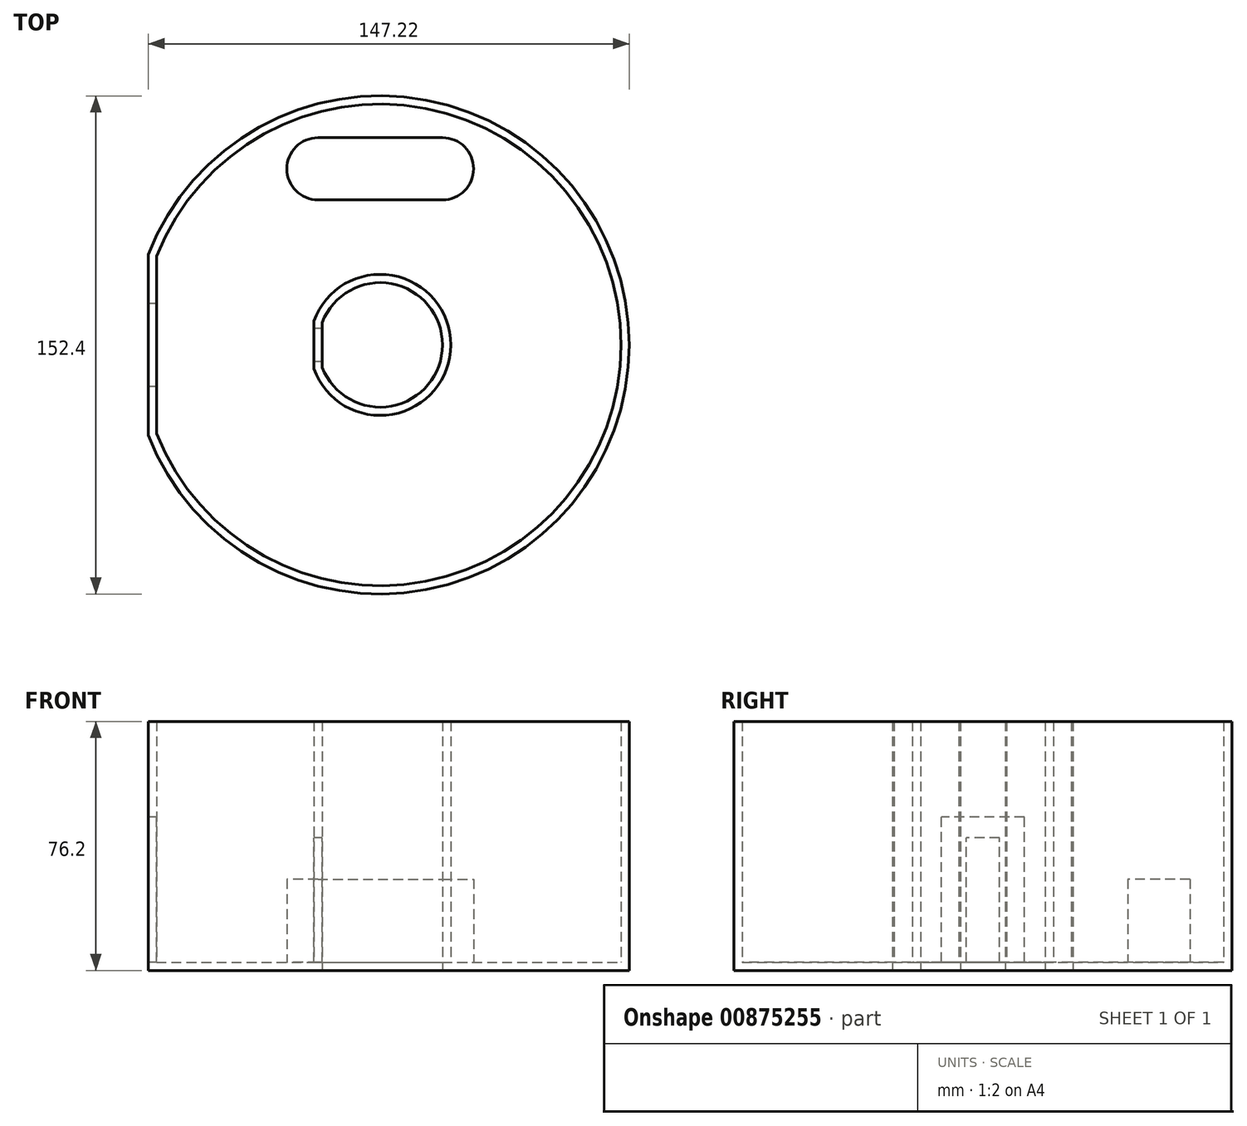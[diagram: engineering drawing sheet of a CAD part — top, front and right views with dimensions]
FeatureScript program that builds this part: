
annotation { "Feature Type Name" : "Feature", "Feature Type Description" : "" }
export const myFeature = defineFeature(function(context is Context, id is Id, definition is map)
    precondition{}
    {
        {
            var Q0;
            Q0=qCreatedBy(makeId("Top.planeOp"),FACE);
            var sketch = newSketch(context, id + "F0", { "sketchPlane" : qUnion([Q0])});
            skCircle(sketch, "E0", {"center": v(0, 0) * mm, "radius": 76.2 * mm});
            skCircle(sketch, "E1", {"center": v(0, 0) * mm, "radius": 19.05 * mm});
            skLineSegment(sketch, "E2", {"start": v(-71.02, 27.6) * mm, "end": v(-71.02, -27.6) * mm});
            skLineSegment(sketch, "E3", {"start": v(-17.77, 6.86) * mm, "end": v(-17.77, -6.86) * mm});
            skPoint(sketch, "E4.endSnap0", {"position": v(-17.77, 0) * mm});
            skSolve(sketch);
        }
        {
            var Q0;
            Q0=makeQuery(id+"F0.imprint","IMPRINT",FACE,{"disambiguationData":[TD([[makeQuery(id+"F0.imprint","IMPRINT",EDGE,{"derivedFrom":sQuery(id+"F0.wireOp",EDGE,"E1")}),-1.0]])]});
            var Q1;
            {var subQ0=sQuery(id+"F0.wireOp",EDGE,"E3");Q1=makeQuery(id+"F0.imprint","IMPRINT",FACE,{"disambiguationData":[TD([[makeQuery(id+"F0.imprint","IMPRINT",EDGE,{"derivedFrom":subQ0}),-1.0]])]});}
            extrude(context, id + "F1", {"entities" : qUnion([Q0, Q1]), "depth" : 76.2 * mm, "offsetDistance" : 25.4 * mm});
        }
        {
            var Q0;
            Q0=makeQuery(id+"F1.opExtrude","CAP_FACE",FACE,{"disambiguationData":[OSD([sQuery(id+"F0.wireOp",EDGE,"E0"),sQuery(id+"F0.wireOp",EDGE,"E1")])],"isStart":false});
            shell(context, id + "F2", {"entities" : qUnion([Q0]), "thickness" : 2.54 * mm});
        }
        {
            var Q0;
            {var subQ0=sQuery(id+"F0.wireOp",EDGE,"E1");var subQ1=sQuery(id+"F0.wireOp",EDGE,"E0");Q0=makeQuery(id+"F2.opShell","OFFSET_FACE",FACE,{"disambiguationData":[OSD([subQ1,subQ0]),TDD([makeQuery(id+"F1.opExtrude","CAP_FACE",FACE,{"disambiguationData":[OSD([subQ1,subQ0])],"isStart":true})])]});}
            var sketch = newSketch(context, id + "F3", { "sketchPlane" : qUnion([Q0])});
            skLineSegment(sketch, "E5.bottom", {"start": v(-19.05, 63.4) * mm, "end": v(19.05, 63.4) * mm});
            skLineSegment(sketch, "E5.top", {"start": v(-19.05, 44.35) * mm, "end": v(19.05, 44.35) * mm});
            skLineSegment(sketch, "E5.left", {"start": v(-19.05, 63.4) * mm, "end": v(-19.05, 44.35) * mm});
            skLineSegment(sketch, "E5.right", {"start": v(19.05, 63.4) * mm, "end": v(19.05, 44.35) * mm});
            skCircle(sketch, "E6", {"center": v(-19.05, 53.88) * mm, "radius": 9.53 * mm});
            skCircle(sketch, "E7", {"center": v(19.05, 53.88) * mm, "radius": 9.53 * mm});
            skLineSegment(sketch, "E8", {"start": v(0, 0) * mm, "end": v(0, 44.35) * mm});
            skLineSegment(sketch, "E9", {"start": v(0, 0) * mm, "end": v(0, -30.53) * mm});
            skSolve(sketch);
        }
        {
            var Q0;
            Q0 = qSketchRegion(id + "F3", true);
            extrude(context, id + "F4", {"entities" : qUnion([Q0]), "operationType" : NewBodyOperationType.ADD, "depth" : 25.4 * mm, "offsetDistance" : 25.4 * mm});
        }
        {
            var Q0;
            Q0=makeQuery(id+"F1.opExtrude","SWEPT_FACE",FACE,{"disambiguationData":[OSD([sQuery(id+"F0.wireOp",EDGE,"E2")])]});
            var sketch = newSketch(context, id + "F5", { "sketchPlane" : qUnion([Q0])});
            skLineSegment(sketch, "E10.bottom", {"start": v(-12.7, 0) * mm, "end": v(12.7, 0) * mm});
            skLineSegment(sketch, "E10.top", {"start": v(-12.7, 2.54) * mm, "end": v(12.7, 2.54) * mm});
            skLineSegment(sketch, "E10.left", {"start": v(-12.7, 0) * mm, "end": v(-12.7, 2.54) * mm});
            skLineSegment(sketch, "E10.right", {"start": v(12.7, 0) * mm, "end": v(12.7, 2.54) * mm});
            skLineSegment(sketch, "E11.top", {"start": v(-12.7, 47) * mm, "end": v(12.7, 47) * mm});
            skLineSegment(sketch, "E11.left", {"start": v(-12.7, 2.54) * mm, "end": v(-12.7, 47) * mm});
            skLineSegment(sketch, "E11.right", {"start": v(12.7, 2.54) * mm, "end": v(12.7, 47) * mm});
            skSolve(sketch);
        }
        {
            var Q0;
            Q0=makeQuery(id+"F5.imprint","IMPRINT",FACE,{"disambiguationData":[TD([[makeQuery(id+"F5.imprint","IMPRINT",EDGE,{"derivedFrom":sQuery(id+"F5.wireOp",EDGE,"E10.top")}),1.0]])]});
            extrude(context, id + "F6", {"entities" : qUnion([Q0]), "operationType" : NewBodyOperationType.REMOVE, "oppositeDirection" : true, "depth" : 2.54 * mm, "offsetDistance" : 25.4 * mm});
        }
        {
            var Q0;
            Q0=makeQuery(id+"F2.opShell","OFFSET_FACE",FACE,{"disambiguationData":[OSD([sQuery(id+"F0.wireOp",EDGE,"E3")])]});
            var sketch = newSketch(context, id + "F7", { "sketchPlane" : qUnion([Q0])});
            skLineSegment(sketch, "E12.bottom", {"start": v(-5.08, 2.54) * mm, "end": v(5.08, 2.54) * mm});
            skLineSegment(sketch, "E12.top", {"start": v(-5.08, 40.64) * mm, "end": v(5.08, 40.64) * mm});
            skLineSegment(sketch, "E12.left", {"start": v(-5.08, 2.54) * mm, "end": v(-5.08, 40.64) * mm});
            skLineSegment(sketch, "E12.right", {"start": v(5.08, 2.54) * mm, "end": v(5.08, 40.64) * mm});
            skLineSegment(sketch, "E13", {"start": v(-7.32, 2.54) * mm, "end": v(-5.08, 2.54) * mm});
            skLineSegment(sketch, "E14", {"start": v(5.08, 2.54) * mm, "end": v(7.32, 2.54) * mm});
            skLineSegment(sketch, "E15", {"start": v(7.32, 2.54) * mm, "end": v(-7.32, 2.54) * mm});
            skSolve(sketch);
        }
        {
            var Q0;
            Q0 = qSketchRegion(id + "F7", true);
            extrude(context, id + "F8", {"entities" : qUnion([Q0]), "operationType" : NewBodyOperationType.REMOVE, "oppositeDirection" : true, "depth" : 2.54 * mm, "offsetDistance" : 25.4 * mm});
        }
    });
